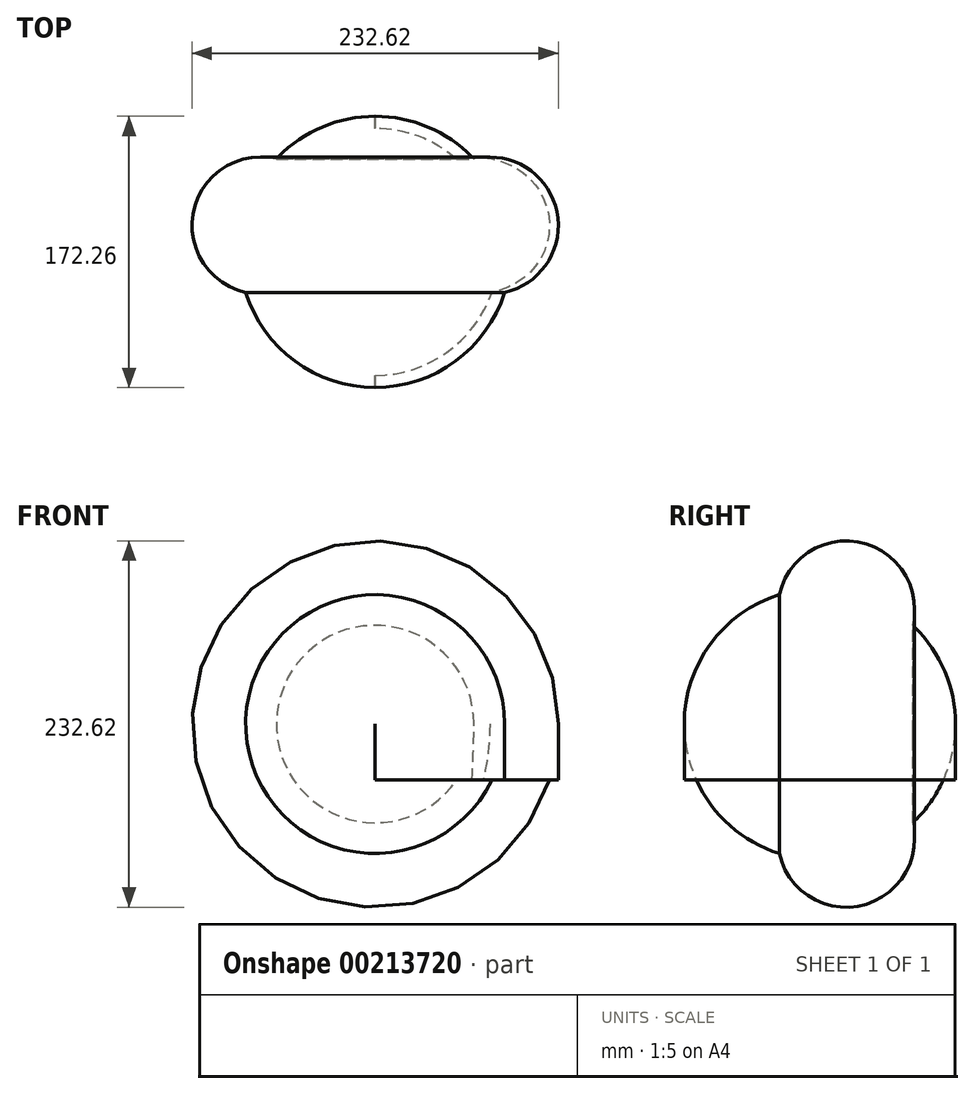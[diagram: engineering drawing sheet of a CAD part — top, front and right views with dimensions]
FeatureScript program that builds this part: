
annotation { "Feature Type Name" : "Feature", "Feature Type Description" : "" }
export const myFeature = defineFeature(function(context is Context, id is Id, definition is map)
    precondition{}
    {
        {
            var Q0;
            Q0=qCreatedBy(makeId("Top.planeOp"),FACE);
            var sketch = newSketch(context, id + "F0", { "sketchPlane" : qUnion([Q0])});
            skArc(sketch, "E0", {"start": v(0, -86.13) * mm, "mid": v(51, -69.41) * mm, "end": v(82.2, -25.75) * mm});
            skArc(sketch, "E1", {"start": v(82.2, -25.75) * mm, "mid": v(115.2, 26.45) * mm, "end": v(62.73, 59.02) * mm});
            skLineSegment(sketch, "E2", {"start": v(0, 86.13) * mm, "end": v(0, -86.13) * mm});
            skArc(sketch, "E3.trimOffspring", {"start": v(62.73, 59.02) * mm, "mid": v(34.17, 79.06) * mm, "end": v(0, 86.13) * mm});
            skSolve(sketch);
        }
        {
            var Q0;
            Q0 = qSketchRegion(id + "F0", true);
            extrude(context, id + "F1", {"entities" : qUnion([Q0]), "depth" : 35.56 * mm});
        }
        {
            var Q0;
            Q0=makeQuery(id+"F1.opExtrude","CAP_FACE",FACE,{"disambiguationData":[OSD([sQuery(id+"F0.wireOp",EDGE,"E0"),sQuery(id+"F0.wireOp",EDGE,"E1"),sQuery(id+"F0.wireOp",EDGE,"E2"),sQuery(id+"F0.wireOp",EDGE,"E3.trimOffspring")])],"isStart":false});
            var Q1;
            Q1=makeQuery(id+"F1.opExtrude","CAP_EDGE",EDGE,{"disambiguationData":[OSD([sQuery(id+"F0.wireOp",EDGE,"E2")])],"isStart":false});
            revolve(context, id + "F2", {"operationType" : NewBodyOperationType.ADD, "entities" : qUnion([Q0]), "axis" : qUnion([Q1]), "revolveType" : RevolveType.FULL});
        }
    });
